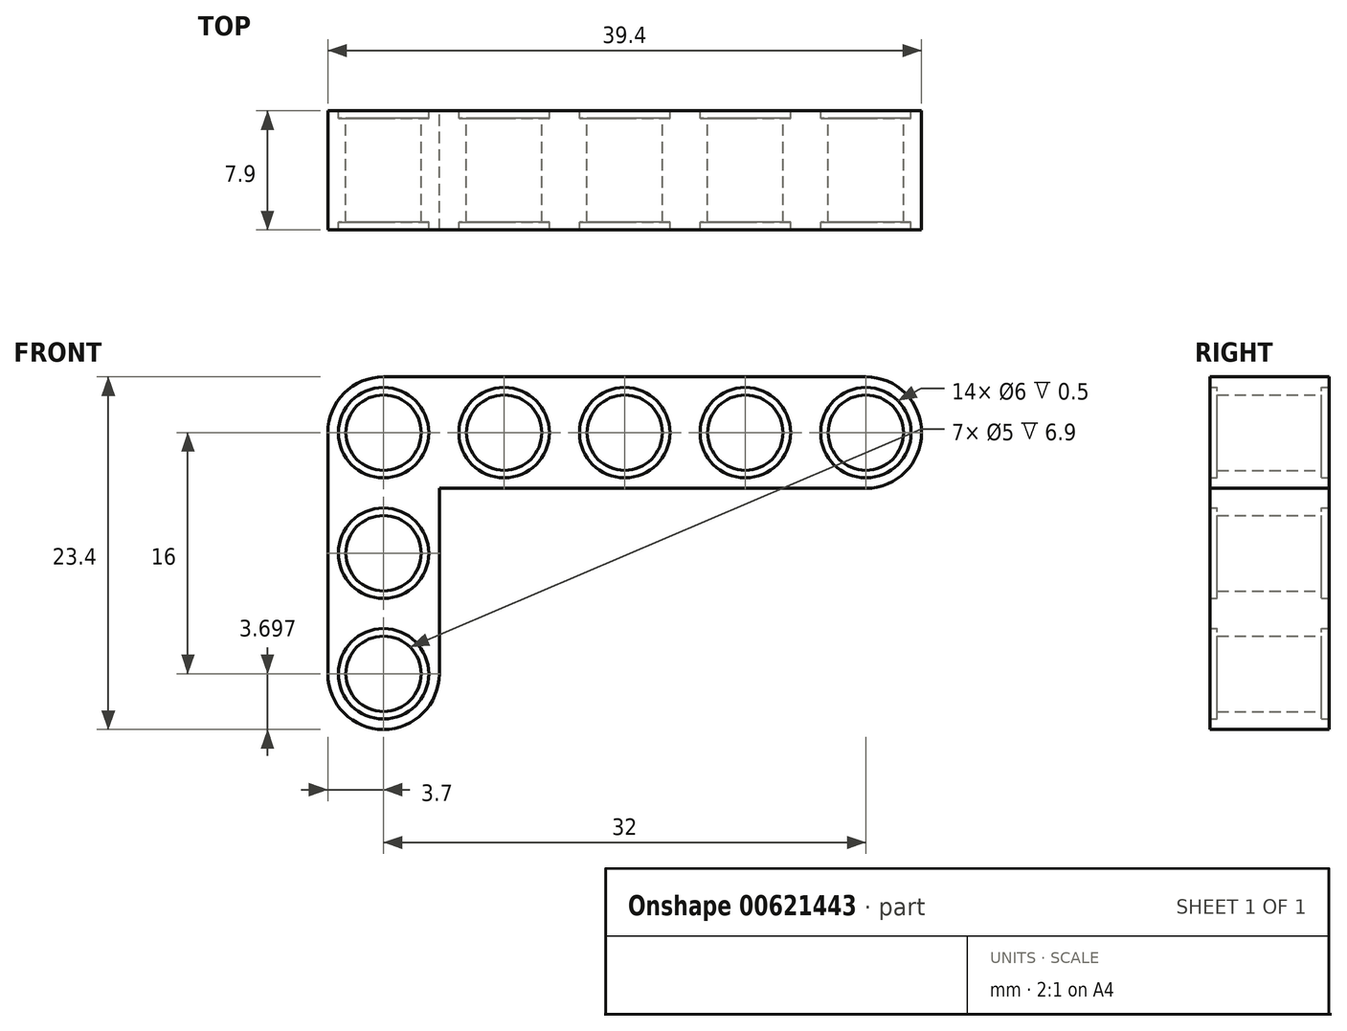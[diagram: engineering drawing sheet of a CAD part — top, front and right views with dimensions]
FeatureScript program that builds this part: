
annotation { "Feature Type Name" : "Feature", "Feature Type Description" : "" }
export const myFeature = defineFeature(function(context is Context, id is Id, definition is map)
    precondition{}
    {
        {
            var Q0;
            Q0=qCreatedBy(makeId("Front.planeOp"),FACE);
            var sketch = newSketch(context, id + "F0", { "sketchPlane" : qUnion([Q0])});
            skLineSegment(sketch, "E0", {"start": v(42.83, -6.91) * mm, "end": v(3.43, -6.91) * mm});
            skLineSegment(sketch, "E1", {"start": v(3.43, -6.91) * mm, "end": v(3.43, -30.31) * mm});
            skLineSegment(sketch, "E2", {"start": v(3.43, -30.31) * mm, "end": v(10.83, -30.31) * mm});
            skLineSegment(sketch, "E3", {"start": v(42.83, -6.91) * mm, "end": v(42.83, -14.31) * mm});
            skLineSegment(sketch, "E4", {"start": v(10.83, -14.31) * mm, "end": v(10.83, -30.31) * mm});
            skLineSegment(sketch, "E5", {"start": v(10.83, -14.31) * mm, "end": v(42.83, -14.31) * mm});
            skCircle(sketch, "E6", {"center": v(39.13, -10.61) * mm, "radius": 3 * mm});
            skCircle(sketch, "E7", {"center": v(31.13, -10.61) * mm, "radius": 3 * mm});
            skCircle(sketch, "E8", {"center": v(23.13, -10.61) * mm, "radius": 3 * mm});
            skCircle(sketch, "E9", {"center": v(15.13, -10.61) * mm, "radius": 3 * mm});
            skCircle(sketch, "E10", {"center": v(7.13, -10.61) * mm, "radius": 3 * mm});
            skCircle(sketch, "E11", {"center": v(7.13, -10.61) * mm, "radius": 2.5 * mm});
            skCircle(sketch, "E12", {"center": v(15.13, -10.61) * mm, "radius": 2.5 * mm});
            skCircle(sketch, "E13", {"center": v(23.13, -10.61) * mm, "radius": 2.5 * mm});
            skCircle(sketch, "E14", {"center": v(31.13, -10.61) * mm, "radius": 2.5 * mm});
            skCircle(sketch, "E15", {"center": v(39.13, -10.61) * mm, "radius": 2.5 * mm});
            skCircle(sketch, "E16", {"center": v(7.13, -26.61) * mm, "radius": 3 * mm});
            skCircle(sketch, "E17", {"center": v(7.13, -26.61) * mm, "radius": 2.5 * mm});
            skCircle(sketch, "E18", {"center": v(7.13, -18.61) * mm, "radius": 3 * mm});
            skCircle(sketch, "E19", {"center": v(7.13, -18.61) * mm, "radius": 2.5 * mm});
            skSolve(sketch);
        }
        {
            var Q0;
            Q0=makeQuery(id+"F0.imprint","IMPRINT",FACE,{"disambiguationData":[TD([[makeQuery(id+"F0.imprint","IMPRINT",EDGE,{"derivedFrom":sQuery(id+"F0.wireOp",EDGE,"E0")}),1.0]])]});
            extrude(context, id + "F1", {"entities" : qUnion([Q0]), "endBound" : BoundingType.SYMMETRIC, "depth" : 7.9 * mm, "offsetDistance" : 25 * mm});
        }
        {
            var Q0;
            Q0=makeQuery(id+"F0.imprint","IMPRINT",FACE,{"disambiguationData":[TD([[makeQuery(id+"F0.imprint","IMPRINT",EDGE,{"derivedFrom":sQuery(id+"F0.wireOp",EDGE,"E6")}),1.0]])]});
            var Q1;
            Q1=makeQuery(id+"F0.imprint","IMPRINT",FACE,{"disambiguationData":[TD([[makeQuery(id+"F0.imprint","IMPRINT",EDGE,{"derivedFrom":sQuery(id+"F0.wireOp",EDGE,"E7")}),1.0]])]});
            var Q2;
            Q2=makeQuery(id+"F0.imprint","IMPRINT",FACE,{"disambiguationData":[TD([[makeQuery(id+"F0.imprint","IMPRINT",EDGE,{"derivedFrom":sQuery(id+"F0.wireOp",EDGE,"E8")}),1.0]])]});
            var Q3;
            Q3=makeQuery(id+"F0.imprint","IMPRINT",FACE,{"disambiguationData":[TD([[makeQuery(id+"F0.imprint","IMPRINT",EDGE,{"derivedFrom":sQuery(id+"F0.wireOp",EDGE,"E9")}),1.0]])]});
            var Q4;
            Q4=makeQuery(id+"F0.imprint","IMPRINT",FACE,{"disambiguationData":[TD([[makeQuery(id+"F0.imprint","IMPRINT",EDGE,{"derivedFrom":sQuery(id+"F0.wireOp",EDGE,"E10")}),1.0]])]});
            var Q5;
            Q5=makeQuery(id+"F0.imprint","IMPRINT",FACE,{"disambiguationData":[TD([[makeQuery(id+"F0.imprint","IMPRINT",EDGE,{"derivedFrom":sQuery(id+"F0.wireOp",EDGE,"E18")}),1.0]])]});
            var Q6;
            Q6=makeQuery(id+"F0.imprint","IMPRINT",FACE,{"disambiguationData":[TD([[makeQuery(id+"F0.imprint","IMPRINT",EDGE,{"derivedFrom":sQuery(id+"F0.wireOp",EDGE,"E16")}),1.0]])]});
            extrude(context, id + "F2", {"entities" : qUnion([Q0, Q1, Q2, Q3, Q4, Q5, Q6]), "operationType" : NewBodyOperationType.ADD, "endBound" : BoundingType.SYMMETRIC, "depth" : 6.9 * mm, "offsetDistance" : 25 * mm});
        }
        {
            var Q0;
            Q0=makeQuery(id+"F1.opExtrude","SWEPT_EDGE",EDGE,{"disambiguationData":[OSD([sQuery(id+"F0.wireOp",EDGE,"E0"),sQuery(id+"F0.wireOp",EDGE,"E3")])]});
            var Q1;
            Q1=makeQuery(id+"F1.opExtrude","SWEPT_EDGE",EDGE,{"disambiguationData":[OSD([sQuery(id+"F0.wireOp",EDGE,"E3"),sQuery(id+"F0.wireOp",EDGE,"E5")])]});
            var Q2;
            Q2=makeQuery(id+"F1.opExtrude","SWEPT_EDGE",EDGE,{"disambiguationData":[OSD([sQuery(id+"F0.wireOp",EDGE,"E2"),sQuery(id+"F0.wireOp",EDGE,"E4")])]});
            var Q3;
            Q3=makeQuery(id+"F1.opExtrude","SWEPT_EDGE",EDGE,{"disambiguationData":[OSD([sQuery(id+"F0.wireOp",EDGE,"E1"),sQuery(id+"F0.wireOp",EDGE,"E2")])]});
            var Q4;
            Q4=makeQuery(id+"F1.opExtrude","SWEPT_EDGE",EDGE,{"disambiguationData":[OSD([sQuery(id+"F0.wireOp",EDGE,"E0"),sQuery(id+"F0.wireOp",EDGE,"E1")])]});
            fillet(context, id + "F3", {"entities" : qUnion([Q0, Q1, Q2, Q3, Q4]), "radius" : 3.7 * mm, "tangentPropagation" : true, "allowEdgeOverflow" : false});
        }
    });
